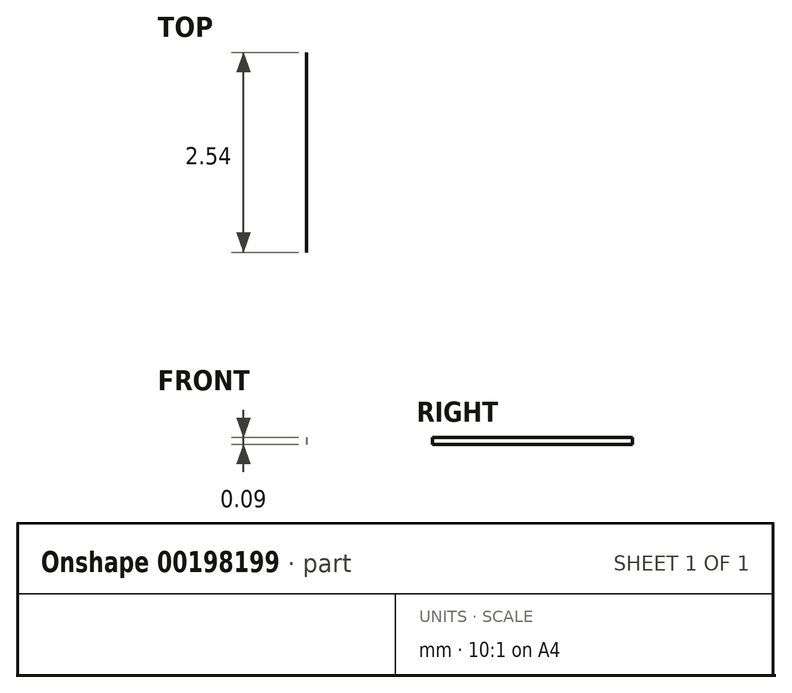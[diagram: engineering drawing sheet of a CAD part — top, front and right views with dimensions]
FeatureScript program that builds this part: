
annotation { "Feature Type Name" : "Feature", "Feature Type Description" : "" }
export const myFeature = defineFeature(function(context is Context, id is Id, definition is map)
    precondition{}
    {
        {
            var Q0;
            Q0=qCreatedBy(makeId("Front.planeOp"),FACE);
            var sketch = newSketch(context, id + "F0", { "sketchPlane" : qUnion([Q0])});
            skCircle(sketch, "E0", {"center": v(0, 0) * mm, "radius": 1.25 * mm});
            skLineSegment(sketch, "E1", {"start": v(-1.25, 0) * mm, "end": v(0, 34.98) * mm});
            skLineSegment(sketch, "E2.MirrorCS", {"start": v(1.25, 0) * mm, "end": v(0, 34.98) * mm});
            skSolve(sketch);
        }
        {
            var Q0;
            {var subQ0=sQuery(id+"F0.wireOp",EDGE,"E2.MirrorCS");var subQ1=sQuery(id+"F0.wireOp",EDGE,"E0");var subQ2=makeQuery(id+"F0.imprint","INTERSECT",VERTEX,{"disambiguationData":[OD(1.0)],"derivedFrom":[subQ1,subQ0]});Q0=makeQuery(id+"F0.imprint","IMPRINT",FACE,{"disambiguationData":[TD([[makeQuery(id+"F0.imprint","IMPRINT",EDGE,{"disambiguationData":[TD([[subQ2,-1.0]])],"derivedFrom":subQ1}),-1.0]])]});}
            var Q1;
            {var subQ0=sQuery(id+"F0.wireOp",EDGE,"E2.MirrorCS");var subQ1=sQuery(id+"F0.wireOp",EDGE,"E0");var subQ2=makeQuery(id+"F0.imprint","INTERSECT",VERTEX,{"disambiguationData":[OD(1.0)],"derivedFrom":[subQ1,subQ0]});Q1=makeQuery(id+"F0.imprint","IMPRINT",FACE,{"disambiguationData":[TD([[makeQuery(id+"F0.imprint","IMPRINT",EDGE,{"disambiguationData":[TD([[subQ2,-1.0]])],"derivedFrom":subQ1}),1.0]])]});}
            extrude(context, id + "F1", {"entities" : qUnion([Q0, Q1]), "depth" : 2.54 * mm});
        }
        {
            var Q0;
            Q0=makeQuery(id+"F1.opExtrude","CAP_FACE",FACE,{"disambiguationData":[OSD([sQuery(id+"F0.wireOp",EDGE,"E0"),sQuery(id+"F0.wireOp",EDGE,"E1"),sQuery(id+"F0.wireOp",EDGE,"E2.MirrorCS")])],"isStart":true});
            var sketch = newSketch(context, id + "F2", { "sketchPlane" : qUnion([Q0])});
            skLineSegment(sketch, "E3", {"start": v(-1.25, 0) * mm, "end": v(1.25, 0) * mm, "construction": true});
            skCircle(sketch, "E4", {"center": v(0, 0) * mm, "radius": 1.19 * mm});
            skSolve(sketch);
        }
        {
            var Q0;
            Q0=qSketchRegion(id+"F2",true);
            extrude(context, id + "F3", {"entities" : qUnion([Q0]), "operationType" : NewBodyOperationType.REMOVE, "oppositeDirection" : true, "depth" : 2.03 * mm});
        }
    });
